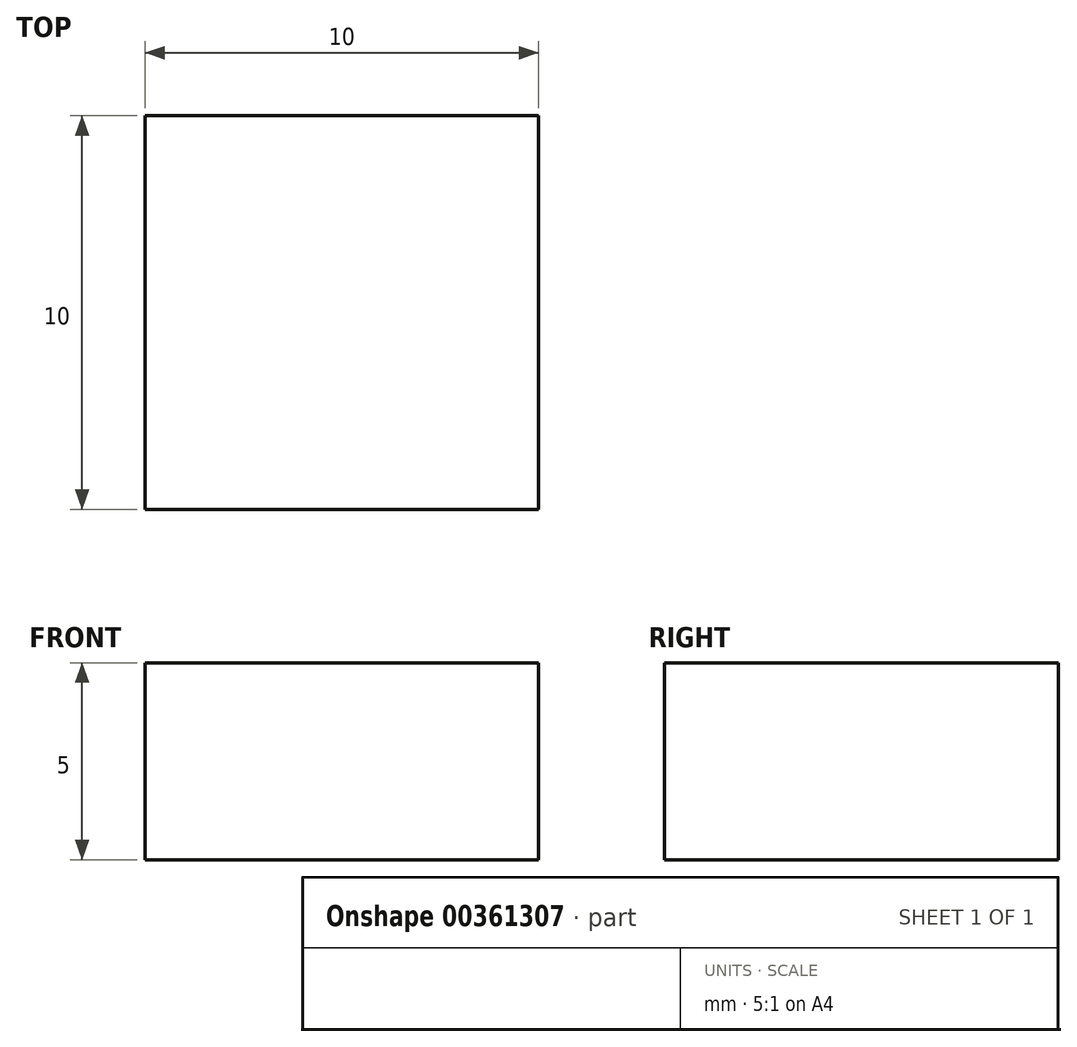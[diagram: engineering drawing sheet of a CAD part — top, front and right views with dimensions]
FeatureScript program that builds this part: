
annotation { "Feature Type Name" : "Feature", "Feature Type Description" : "" }
export const myFeature = defineFeature(function(context is Context, id is Id, definition is map)
    precondition{}
    {
        {
            var Q0;
            Q0=qCreatedBy(makeId("Top.planeOp"),FACE);
            var sketch = newSketch(context, id + "F0", { "sketchPlane" : qUnion([Q0])});
            skLineSegment(sketch, "E0.bottom", {"start": v(0, 0) * mm, "end": v(10, 0) * mm});
            skLineSegment(sketch, "E0.top", {"start": v(0, -10) * mm, "end": v(10, -10) * mm});
            skLineSegment(sketch, "E0.left", {"start": v(0, 0) * mm, "end": v(0, -10) * mm});
            skLineSegment(sketch, "E0.right", {"start": v(10, 0) * mm, "end": v(10, -10) * mm});
            skSolve(sketch);
        }
        {
            var Q0;
            Q0=makeQuery(id+"F0.imprint","IMPRINT",FACE,{"disambiguationData":[TD([[makeQuery(id+"F0.imprint","IMPRINT",EDGE,{"derivedFrom":sQuery(id+"F0.wireOp",EDGE,"E0.bottom")}),-1.0]])]});
            extrude(context, id + "F1", {"entities" : qUnion([Q0]), "depth" : 5 * mm});
        }
    });
